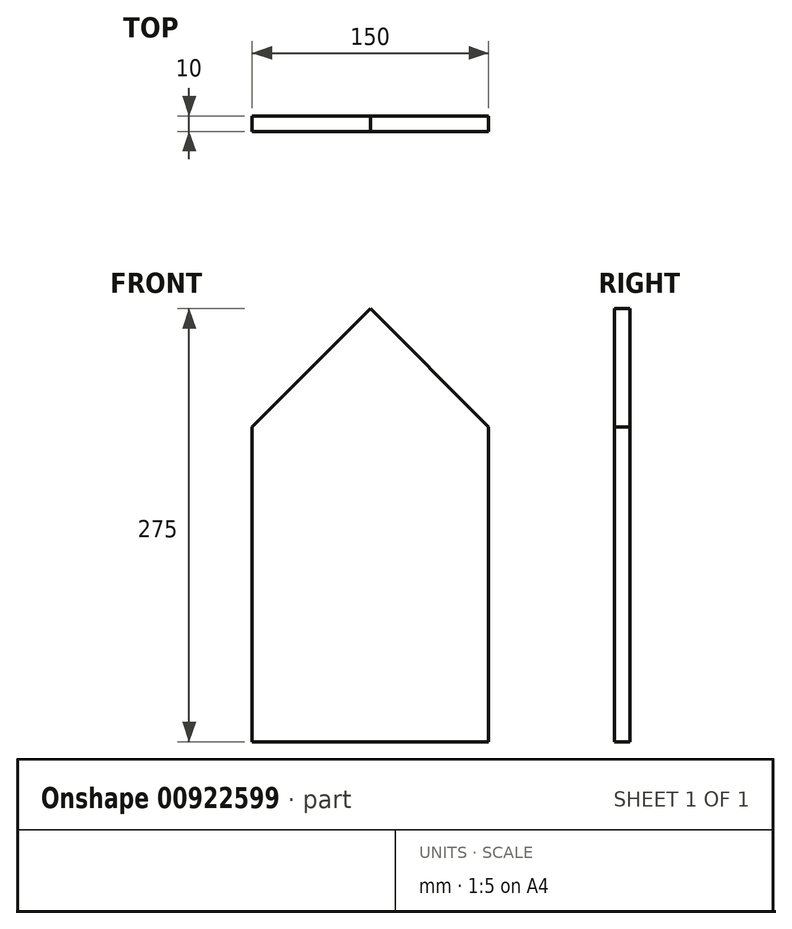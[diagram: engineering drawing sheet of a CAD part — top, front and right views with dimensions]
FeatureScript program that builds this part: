
annotation { "Feature Type Name" : "Feature", "Feature Type Description" : "" }
export const myFeature = defineFeature(function(context is Context, id is Id, definition is map)
    precondition{}
    {
        {
            var Q0;
            Q0=qCreatedBy(makeId("Front.planeOp"),FACE);
            var sketch = newSketch(context, id + "F0", { "sketchPlane" : qUnion([Q0])});
            skLineSegment(sketch, "E0.bottom", {"start": v(75, 100) * mm, "end": v(-75, 100) * mm});
            skLineSegment(sketch, "E0.top", {"start": v(75, -100) * mm, "end": v(-75, -100) * mm});
            skLineSegment(sketch, "E0.left", {"start": v(75, 100) * mm, "end": v(75, -100) * mm});
            skLineSegment(sketch, "E0.right", {"start": v(-75, 100) * mm, "end": v(-75, -100) * mm});
            skPoint(sketch, "E0.middle", {"position": v(0, 0) * mm});
            skLineSegment(sketch, "E1", {"start": v(0, 100) * mm, "end": v(0, 175) * mm});
            skLineSegment(sketch, "E2", {"start": v(0, 175) * mm, "end": v(-75, 100) * mm});
            skLineSegment(sketch, "E3", {"start": v(0, 175) * mm, "end": v(75, 100) * mm});
            skSolve(sketch);
        }
        {
            var Q0;
            Q0 = qSketchRegion(id + "F0", true);
            extrude(context, id + "F1", {"entities" : qUnion([Q0]), "depth" : 10 * mm, "offsetDistance" : 25.4 * mm});
        }
    });
